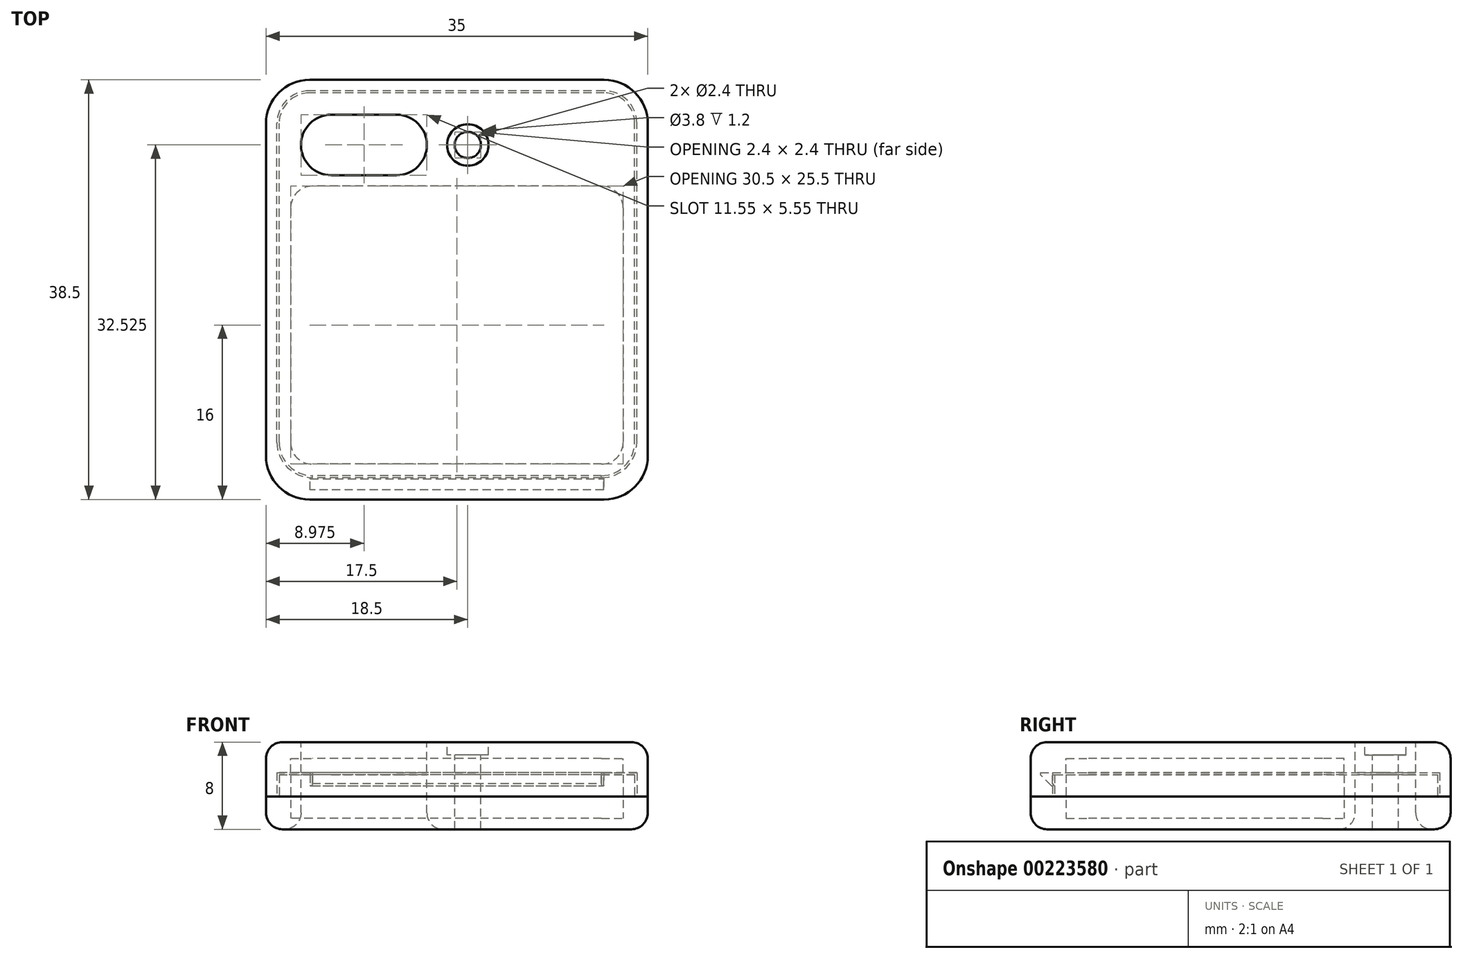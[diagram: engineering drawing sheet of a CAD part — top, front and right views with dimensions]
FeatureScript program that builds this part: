
annotation { "Feature Type Name" : "Feature", "Feature Type Description" : "" }
export const myFeature = defineFeature(function(context is Context, id is Id, definition is map)
    precondition{}
    {
        {
            var Q0;
            Q0=qCreatedBy(makeId("Top.planeOp"),FACE);
            var sketch = newSketch(context, id + "F0", { "sketchPlane" : qUnion([Q0])});
            skLineSegment(sketch, "E0.bottom", {"start": v(15, 12.5) * mm, "end": v(-15, 12.5) * mm, "construction": true});
            skLineSegment(sketch, "E0.top", {"start": v(15, -12.5) * mm, "end": v(-15, -12.5) * mm, "construction": true});
            skLineSegment(sketch, "E0.left", {"start": v(15, 12.5) * mm, "end": v(15, -12.5) * mm, "construction": true});
            skLineSegment(sketch, "E0.right", {"start": v(-15, 12.5) * mm, "end": v(-15, -12.5) * mm, "construction": true});
            skPoint(sketch, "E0.middle", {"position": v(0, 0) * mm});
            skLineSegment(sketch, "E1.bottom", {"start": v(13.5, -16) * mm, "end": v(-13.5, -16) * mm});
            skLineSegment(sketch, "E1.top", {"start": v(13.5, 22.5) * mm, "end": v(-13.5, 22.5) * mm});
            skLineSegment(sketch, "E1.left", {"start": v(17.5, -12) * mm, "end": v(17.5, 18.5) * mm});
            skLineSegment(sketch, "E1.right", {"start": v(-17.5, -12) * mm, "end": v(-17.5, 18.5) * mm});
            skPoint(sketch, "E1.middle", {"position": v(0, 3.25) * mm});
            skLineSegment(sketch, "E2.bottom", {"start": v(13.25, 12.75) * mm, "end": v(-13.25, 12.75) * mm});
            skLineSegment(sketch, "E2.top", {"start": v(13.25, -12.75) * mm, "end": v(-13.25, -12.75) * mm});
            skLineSegment(sketch, "E2.left", {"start": v(15.25, 10.75) * mm, "end": v(15.25, -10.75) * mm});
            skLineSegment(sketch, "E2.right", {"start": v(-15.25, 10.75) * mm, "end": v(-15.25, -10.75) * mm});
            skPoint(sketch, "E3.visualSharp", {"position": v(15.25, -12.75) * mm});
            skArc(sketch, "E3.filletArc", {"start": v(13.25, -12.75) * mm, "mid": v(14.66, -12.16) * mm, "end": v(15.25, -10.75) * mm});
            skPoint(sketch, "E4.visualSharp", {"position": v(-15.25, -12.75) * mm});
            skArc(sketch, "E4.filletArc", {"start": v(-15.25, -10.75) * mm, "mid": v(-14.66, -12.16) * mm, "end": v(-13.25, -12.75) * mm});
            skPoint(sketch, "E5.visualSharp", {"position": v(15.25, 12.75) * mm});
            skArc(sketch, "E5.filletArc", {"start": v(15.25, 10.75) * mm, "mid": v(14.66, 12.16) * mm, "end": v(13.25, 12.75) * mm});
            skPoint(sketch, "E6.visualSharp", {"position": v(-15.25, 12.75) * mm});
            skArc(sketch, "E6.filletArc", {"start": v(-13.25, 12.75) * mm, "mid": v(-14.66, 12.16) * mm, "end": v(-15.25, 10.75) * mm});
            skPoint(sketch, "E7.visualSharp", {"position": v(-17.5, -16) * mm});
            skArc(sketch, "E7.filletArc", {"start": v(-17.5, -12) * mm, "mid": v(-16.33, -14.83) * mm, "end": v(-13.5, -16) * mm});
            skPoint(sketch, "E8.visualSharp", {"position": v(17.5, -16) * mm});
            skArc(sketch, "E8.filletArc", {"start": v(13.5, -16) * mm, "mid": v(16.33, -14.83) * mm, "end": v(17.5, -12) * mm});
            skPoint(sketch, "E9.visualSharp", {"position": v(17.5, 22.5) * mm});
            skArc(sketch, "E9.filletArc", {"start": v(17.5, 18.5) * mm, "mid": v(16.33, 21.33) * mm, "end": v(13.5, 22.5) * mm});
            skPoint(sketch, "E10.visualSharp", {"position": v(-17.5, 22.5) * mm});
            skArc(sketch, "E10.filletArc", {"start": v(-13.5, 22.5) * mm, "mid": v(-16.33, 21.33) * mm, "end": v(-17.5, 18.5) * mm});
            skSolve(sketch);
        }
        {
            var Q0;
            Q0 = qSketchRegion(id + "F0", true);
            extrude(context, id + "F1", {"entities" : qUnion([Q0]), "depth" : 2 * mm});
        }
        {
            var Q0;
            Q0=makeQuery(id+"F1.opExtrude","CAP_FACE",FACE,{"disambiguationData":[OSD([sQuery(id+"F0.wireOp",EDGE,"E1.bottom"),sQuery(id+"F0.wireOp",EDGE,"E1.top"),sQuery(id+"F0.wireOp",EDGE,"E1.left"),sQuery(id+"F0.wireOp",EDGE,"E1.right"),sQuery(id+"F0.wireOp",EDGE,"E2.bottom"),sQuery(id+"F0.wireOp",EDGE,"E2.top"),sQuery(id+"F0.wireOp",EDGE,"E2.left"),sQuery(id+"F0.wireOp",EDGE,"E2.right"),sQuery(id+"F0.wireOp",EDGE,"E3.filletArc"),sQuery(id+"F0.wireOp",EDGE,"E4.filletArc"),sQuery(id+"F0.wireOp",EDGE,"E5.filletArc"),sQuery(id+"F0.wireOp",EDGE,"E6.filletArc"),sQuery(id+"F0.wireOp",EDGE,"E7.filletArc"),sQuery(id+"F0.wireOp",EDGE,"E8.filletArc"),sQuery(id+"F0.wireOp",EDGE,"E9.filletArc"),sQuery(id+"F0.wireOp",EDGE,"E10.filletArc")])],"isStart":true});
            var sketch = newSketch(context, id + "F2", { "sketchPlane" : qUnion([Q0])});
            skArc(sketch, "E11.0", {"start": v(17.5, -18.5) * mm, "mid": v(16.33, -21.33) * mm, "end": v(13.5, -22.5) * mm});
            skLineSegment(sketch, "E11.1", {"start": v(17.5, 12) * mm, "end": v(17.5, -18.5) * mm});
            skLineSegment(sketch, "E11.2", {"start": v(13.5, -22.5) * mm, "end": v(-13.5, -22.5) * mm});
            skArc(sketch, "E11.3", {"start": v(13.5, 16) * mm, "mid": v(16.33, 14.83) * mm, "end": v(17.5, 12) * mm});
            skArc(sketch, "E11.4", {"start": v(-13.5, -22.5) * mm, "mid": v(-16.33, -21.33) * mm, "end": v(-17.5, -18.5) * mm});
            skLineSegment(sketch, "E11.5", {"start": v(-17.5, 12) * mm, "end": v(-17.5, -18.5) * mm});
            skArc(sketch, "E11.6", {"start": v(-17.5, 12) * mm, "mid": v(-16.33, 14.83) * mm, "end": v(-13.5, 16) * mm});
            skLineSegment(sketch, "E11.7", {"start": v(13.5, 16) * mm, "end": v(-13.5, 16) * mm});
            skSolve(sketch);
        }
        {
            var Q0;
            Q0 = qSketchRegion(id + "F2", true);
            extrude(context, id + "F3", {"entities" : qUnion([Q0]), "operationType" : NewBodyOperationType.ADD, "depth" : 1 * mm});
        }
        {
            var Q0;
            Q0=makeQuery(id+"F1.opExtrude","CAP_FACE",FACE,{"disambiguationData":[OSD([sQuery(id+"F0.wireOp",EDGE,"E1.bottom"),sQuery(id+"F0.wireOp",EDGE,"E1.top"),sQuery(id+"F0.wireOp",EDGE,"E1.left"),sQuery(id+"F0.wireOp",EDGE,"E1.right"),sQuery(id+"F0.wireOp",EDGE,"E2.bottom"),sQuery(id+"F0.wireOp",EDGE,"E2.top"),sQuery(id+"F0.wireOp",EDGE,"E2.left"),sQuery(id+"F0.wireOp",EDGE,"E2.right"),sQuery(id+"F0.wireOp",EDGE,"E3.filletArc"),sQuery(id+"F0.wireOp",EDGE,"E4.filletArc"),sQuery(id+"F0.wireOp",EDGE,"E5.filletArc"),sQuery(id+"F0.wireOp",EDGE,"E6.filletArc"),sQuery(id+"F0.wireOp",EDGE,"E7.filletArc"),sQuery(id+"F0.wireOp",EDGE,"E8.filletArc"),sQuery(id+"F0.wireOp",EDGE,"E9.filletArc"),sQuery(id+"F0.wireOp",EDGE,"E10.filletArc")])],"isStart":false});
            var sketch = newSketch(context, id + "F4", { "sketchPlane" : qUnion([Q0])});
            skArc(sketch, "E12.0", {"start": v(16.3, 18.5) * mm, "mid": v(15.48, 20.48) * mm, "end": v(13.5, 21.3) * mm});
            skLineSegment(sketch, "E12.1", {"start": v(16.3, -10.75) * mm, "end": v(16.3, 18.5) * mm});
            skLineSegment(sketch, "E12.2", {"start": v(13.5, 21.3) * mm, "end": v(-13.5, 21.3) * mm});
            skArc(sketch, "E12.4", {"start": v(-13.5, 21.3) * mm, "mid": v(-15.48, 20.48) * mm, "end": v(-16.3, 18.5) * mm});
            skLineSegment(sketch, "E12.5", {"start": v(-16.3, -10.75) * mm, "end": v(-16.3, 18.5) * mm});
            skArc(sketch, "E13.0", {"start": v(15.25, 10.75) * mm, "mid": v(14.66, 12.16) * mm, "end": v(13.25, 12.75) * mm});
            skLineSegment(sketch, "E13.1", {"start": v(15.25, 10.75) * mm, "end": v(15.25, -10.75) * mm});
            skLineSegment(sketch, "E13.2", {"start": v(13.25, 12.75) * mm, "end": v(-13.25, 12.75) * mm});
            skArc(sketch, "E13.3", {"start": v(13.25, -12.75) * mm, "mid": v(14.66, -12.16) * mm, "end": v(15.25, -10.75) * mm});
            skArc(sketch, "E13.4", {"start": v(-13.25, 12.75) * mm, "mid": v(-14.66, 12.16) * mm, "end": v(-15.25, 10.75) * mm});
            skLineSegment(sketch, "E13.5", {"start": v(-15.25, 10.75) * mm, "end": v(-15.25, -10.75) * mm});
            skArc(sketch, "E13.6", {"start": v(-15.25, -10.75) * mm, "mid": v(-14.66, -12.16) * mm, "end": v(-13.25, -12.75) * mm});
            skLineSegment(sketch, "E13.7", {"start": v(13.25, -12.75) * mm, "end": v(-13.25, -12.75) * mm});
            skArc(sketch, "E14.0", {"start": v(13.25, -13.8) * mm, "mid": v(15.4, -12.9) * mm, "end": v(16.3, -10.75) * mm});
            skLineSegment(sketch, "E14.1", {"start": v(13.25, -13.8) * mm, "end": v(-13.25, -13.8) * mm});
            skArc(sketch, "E14.2", {"start": v(-16.3, -10.75) * mm, "mid": v(-15.4, -12.9) * mm, "end": v(-13.25, -13.8) * mm});
            skSolve(sketch);
        }
        {
            var Q0;
            Q0 = qSketchRegion(id + "F4", true);
            extrude(context, id + "F5", {"entities" : qUnion([Q0]), "operationType" : NewBodyOperationType.ADD, "depth" : 2 * mm});
        }
        {
            var Q0;
            Q0=makeQuery(id+"F5.opExtrude","SWEPT_FACE",FACE,{"disambiguationData":[OSD([sQuery(id+"F4.wireOp",EDGE,"E14.1")])]});
            var sketch = newSketch(context, id + "F6", { "sketchPlane" : qUnion([Q0])});
            skLineSegment(sketch, "E15.bottom", {"start": v(-13.25, 4) * mm, "end": v(13.25, 4) * mm});
            skLineSegment(sketch, "E15.top", {"start": v(-13.25, 3) * mm, "end": v(13.25, 3) * mm});
            skLineSegment(sketch, "E15.left", {"start": v(-13.25, 4) * mm, "end": v(-13.25, 3) * mm});
            skLineSegment(sketch, "E15.right", {"start": v(13.25, 4) * mm, "end": v(13.25, 3) * mm});
            skSolve(sketch);
        }
        {
            var Q0;
            Q0 = qSketchRegion(id + "F6", true);
            extrude(context, id + "F7", {"entities" : qUnion([Q0]), "operationType" : NewBodyOperationType.ADD, "depth" : .5 * mm});
        }
        {
            var Q0;
            Q0=makeQuery(id+"F7.opExtrude","CAP_EDGE",EDGE,{"disambiguationData":[OSD([sQuery(id+"F6.wireOp",EDGE,"E15.top")])],"isStart":false});
            chamfer(context, id + "F8", {"entities" : qUnion([Q0]), "width" : .5 * mm, "tangentPropagation" : true});
        }
        {
            var Q0;
            Q0=makeQuery(id+"F1.opExtrude","CAP_FACE",FACE,{"disambiguationData":[OSD([sQuery(id+"F0.wireOp",EDGE,"E1.bottom"),sQuery(id+"F0.wireOp",EDGE,"E1.top"),sQuery(id+"F0.wireOp",EDGE,"E1.left"),sQuery(id+"F0.wireOp",EDGE,"E1.right"),sQuery(id+"F0.wireOp",EDGE,"E2.bottom"),sQuery(id+"F0.wireOp",EDGE,"E2.top"),sQuery(id+"F0.wireOp",EDGE,"E2.left"),sQuery(id+"F0.wireOp",EDGE,"E2.right"),sQuery(id+"F0.wireOp",EDGE,"E3.filletArc"),sQuery(id+"F0.wireOp",EDGE,"E4.filletArc"),sQuery(id+"F0.wireOp",EDGE,"E5.filletArc"),sQuery(id+"F0.wireOp",EDGE,"E6.filletArc"),sQuery(id+"F0.wireOp",EDGE,"E7.filletArc"),sQuery(id+"F0.wireOp",EDGE,"E8.filletArc"),sQuery(id+"F0.wireOp",EDGE,"E9.filletArc"),sQuery(id+"F0.wireOp",EDGE,"E10.filletArc")])],"isStart":false});
            var sketch = newSketch(context, id + "F9", { "sketchPlane" : qUnion([Q0])});
            skLineSegment(sketch, "E16.0", {"start": v(-17.5, -12) * mm, "end": v(-17.5, 18.5) * mm});
            skArc(sketch, "E16.1", {"start": v(-13.5, 22.5) * mm, "mid": v(-16.33, 21.33) * mm, "end": v(-17.5, 18.5) * mm});
            skArc(sketch, "E16.2", {"start": v(-17.5, -12) * mm, "mid": v(-16.33, -14.83) * mm, "end": v(-13.5, -16) * mm});
            skLineSegment(sketch, "E16.3", {"start": v(13.5, 22.5) * mm, "end": v(-13.5, 22.5) * mm});
            skLineSegment(sketch, "E16.4", {"start": v(13.5, -16) * mm, "end": v(-13.5, -16) * mm});
            skArc(sketch, "E16.5", {"start": v(13.5, -16) * mm, "mid": v(16.33, -14.83) * mm, "end": v(17.5, -12) * mm});
            skLineSegment(sketch, "E16.6", {"start": v(17.5, -12) * mm, "end": v(17.5, 18.5) * mm});
            skArc(sketch, "E16.7", {"start": v(17.5, 18.5) * mm, "mid": v(16.33, 21.33) * mm, "end": v(13.5, 22.5) * mm});
            skLineSegment(sketch, "E17.0", {"start": v(-16.5, -10.75) * mm, "end": v(-16.5, 18.5) * mm});
            skArc(sketch, "E17.1", {"start": v(-13.5, 21.5) * mm, "mid": v(-15.62, 20.62) * mm, "end": v(-16.5, 18.5) * mm});
            skArc(sketch, "E17.2", {"start": v(-16.5, -10.75) * mm, "mid": v(-15.55, -13.05) * mm, "end": v(-13.25, -14) * mm});
            skLineSegment(sketch, "E17.3", {"start": v(13.5, 21.5) * mm, "end": v(-13.5, 21.5) * mm});
            skLineSegment(sketch, "E17.4", {"start": v(13.25, -14) * mm, "end": v(-13.25, -14) * mm});
            skArc(sketch, "E17.5", {"start": v(13.25, -14) * mm, "mid": v(15.55, -13.05) * mm, "end": v(16.5, -10.75) * mm});
            skLineSegment(sketch, "E17.6", {"start": v(16.5, -10.75) * mm, "end": v(16.5, 18.5) * mm});
            skArc(sketch, "E17.7", {"start": v(16.5, 18.5) * mm, "mid": v(15.62, 20.62) * mm, "end": v(13.5, 21.5) * mm});
            skSolve(sketch);
        }
        {
            var Q0;
            Q0 = qSketchRegion(id + "F9", true);
            extrude(context, id + "F10", {"entities" : qUnion([Q0]), "depth" : 3.5 * mm});
        }
        {
            var Q0;
            {var subQ2=sQuery(id+"F9.wireOp",EDGE,"E17.4");Q0=makeQuery(id+"F10.boolean.opBoolean","SPLIT",FACE,{"disambiguationData":[TD([makeQuery(id+"F7.opExtrude","SWEPT_FACE",FACE,{"disambiguationData":[OSD([sQuery(id+"F6.wireOp",EDGE,"E15.bottom")])]})])],"derivedFrom":makeQuery(id+"F10.opExtrude","SWEPT_FACE",FACE,{"disambiguationData":[OSD([subQ2])]})});}
            var sketch = newSketch(context, id + "F11", { "sketchPlane" : qUnion([Q0])});
            skLineSegment(sketch, "E18.0", {"start": v(13.45, 4.2) * mm, "end": v(13.45, 3) * mm});
            skLineSegment(sketch, "E18.1", {"start": v(-13.45, 4.2) * mm, "end": v(13.45, 4.2) * mm});
            skLineSegment(sketch, "E18.2", {"start": v(-13.45, 4.2) * mm, "end": v(-13.45, 3) * mm});
            skLineSegment(sketch, "E19", {"start": v(-13.45, 3) * mm, "end": v(13.45, 3) * mm});
            skSolve(sketch);
        }
        {
            var Q0;
            Q0 = qSketchRegion(id + "F11", true);
            extrude(context, id + "F12", {"entities" : qUnion([Q0]), "operationType" : NewBodyOperationType.REMOVE, "oppositeDirection" : true, "depth" : 1.1 * mm});
        }
        {
            var Q0;
            Q0=makeQuery(id+"F12.boolean.opBoolean","COPY",EDGE,{"derivedFrom":makeQuery(id+"F12.opExtrude","CAP_EDGE",EDGE,{"disambiguationData":[OSD([sQuery(id+"F11.wireOp",EDGE,"E19")])],"isStart":false})});
            chamfer(context, id + "F13", {"entities" : qUnion([Q0]), "width" : 1 * mm, "tangentPropagation" : true});
        }
        {
            var Q0;
            Q0=makeQuery(id+"F10.opExtrude","CAP_FACE",FACE,{"disambiguationData":[OSD([sQuery(id+"F9.wireOp",EDGE,"E16.0"),sQuery(id+"F9.wireOp",EDGE,"E16.1"),sQuery(id+"F9.wireOp",EDGE,"E16.2"),sQuery(id+"F9.wireOp",EDGE,"E16.3"),sQuery(id+"F9.wireOp",EDGE,"E16.4"),sQuery(id+"F9.wireOp",EDGE,"E16.5"),sQuery(id+"F9.wireOp",EDGE,"E16.6"),sQuery(id+"F9.wireOp",EDGE,"E16.7"),sQuery(id+"F9.wireOp",EDGE,"E17.0"),sQuery(id+"F9.wireOp",EDGE,"E17.1"),sQuery(id+"F9.wireOp",EDGE,"E17.2"),sQuery(id+"F9.wireOp",EDGE,"E17.3"),sQuery(id+"F9.wireOp",EDGE,"E17.4"),sQuery(id+"F9.wireOp",EDGE,"E17.5"),sQuery(id+"F9.wireOp",EDGE,"E17.6"),sQuery(id+"F9.wireOp",EDGE,"E17.7")])],"isStart":false});
            var sketch = newSketch(context, id + "F14", { "sketchPlane" : qUnion([Q0])});
            skArc(sketch, "E20.0", {"start": v(16.5, 18.5) * mm, "mid": v(15.62, 20.62) * mm, "end": v(13.5, 21.5) * mm});
            skLineSegment(sketch, "E20.1", {"start": v(16.5, -10.75) * mm, "end": v(16.5, 18.5) * mm});
            skLineSegment(sketch, "E20.2", {"start": v(13.5, 21.5) * mm, "end": v(-13.5, 21.5) * mm});
            skArc(sketch, "E20.3", {"start": v(13.25, -14) * mm, "mid": v(15.55, -13.05) * mm, "end": v(16.5, -10.75) * mm});
            skArc(sketch, "E20.4", {"start": v(-13.5, 21.5) * mm, "mid": v(-15.62, 20.62) * mm, "end": v(-16.5, 18.5) * mm});
            skLineSegment(sketch, "E20.5", {"start": v(-16.5, -10.75) * mm, "end": v(-16.5, 18.5) * mm});
            skArc(sketch, "E20.6", {"start": v(-16.5, -10.75) * mm, "mid": v(-15.55, -13.05) * mm, "end": v(-13.25, -14) * mm});
            skLineSegment(sketch, "E20.7", {"start": v(13.25, -14) * mm, "end": v(-13.25, -14) * mm});
            skArc(sketch, "E21.0", {"start": v(15.25, 10.75) * mm, "mid": v(14.66, 12.16) * mm, "end": v(13.25, 12.75) * mm});
            skLineSegment(sketch, "E21.1", {"start": v(15.25, 10.75) * mm, "end": v(15.25, -10.75) * mm});
            skLineSegment(sketch, "E21.2", {"start": v(13.25, 12.75) * mm, "end": v(-13.25, 12.75) * mm});
            skArc(sketch, "E21.3", {"start": v(13.25, -12.75) * mm, "mid": v(14.66, -12.16) * mm, "end": v(15.25, -10.75) * mm});
            skArc(sketch, "E21.4", {"start": v(-13.25, 12.75) * mm, "mid": v(-14.66, 12.16) * mm, "end": v(-15.25, 10.75) * mm});
            skLineSegment(sketch, "E21.5", {"start": v(-15.25, 10.75) * mm, "end": v(-15.25, -10.75) * mm});
            skArc(sketch, "E21.6", {"start": v(-15.25, -10.75) * mm, "mid": v(-14.66, -12.16) * mm, "end": v(-13.25, -12.75) * mm});
            skLineSegment(sketch, "E21.7", {"start": v(13.25, -12.75) * mm, "end": v(-13.25, -12.75) * mm});
            skSolve(sketch);
        }
        {
            var Q0;
            Q0 = qSketchRegion(id + "F14", true);
            var Q1;
            Q1=makeQuery(id+"F12.boolean.opBoolean","COPY",FACE,{"derivedFrom":makeQuery(id+"F12.opExtrude","SWEPT_FACE",FACE,{"disambiguationData":[OSD([sQuery(id+"F11.wireOp",EDGE,"E18.1")])]})});
            extrude(context, id + "F15", {"entities" : qUnion([Q0]), "operationType" : NewBodyOperationType.ADD, "endBound" : BoundingType.UP_TO_SURFACE, "oppositeDirection" : true, "endBoundEntityFace" : qUnion([Q1]), "depth" : 25 * mm});
        }
        {
            var Q0;
            Q0=makeQuery(id+"F15.boolean.opBoolean","MERGE",FACE,{"derivedFrom":[makeQuery(id+"F10.opExtrude","CAP_FACE",FACE,{"disambiguationData":[OSD([sQuery(id+"F9.wireOp",EDGE,"E16.0"),sQuery(id+"F9.wireOp",EDGE,"E16.1"),sQuery(id+"F9.wireOp",EDGE,"E16.2"),sQuery(id+"F9.wireOp",EDGE,"E16.3"),sQuery(id+"F9.wireOp",EDGE,"E16.4"),sQuery(id+"F9.wireOp",EDGE,"E16.5"),sQuery(id+"F9.wireOp",EDGE,"E16.6"),sQuery(id+"F9.wireOp",EDGE,"E16.7"),sQuery(id+"F9.wireOp",EDGE,"E17.0"),sQuery(id+"F9.wireOp",EDGE,"E17.1"),sQuery(id+"F9.wireOp",EDGE,"E17.2"),sQuery(id+"F9.wireOp",EDGE,"E17.3"),sQuery(id+"F9.wireOp",EDGE,"E17.4"),sQuery(id+"F9.wireOp",EDGE,"E17.5"),sQuery(id+"F9.wireOp",EDGE,"E17.6"),sQuery(id+"F9.wireOp",EDGE,"E17.7")])],"isStart":false}),makeQuery(id+"F15.opExtrude","CAP_FACE",FACE,{"disambiguationData":[OSD([sQuery(id+"F14.wireOp",EDGE,"E20.0"),sQuery(id+"F14.wireOp",EDGE,"E20.1"),sQuery(id+"F14.wireOp",EDGE,"E20.2"),sQuery(id+"F14.wireOp",EDGE,"E20.3"),sQuery(id+"F14.wireOp",EDGE,"E20.4"),sQuery(id+"F14.wireOp",EDGE,"E20.5"),sQuery(id+"F14.wireOp",EDGE,"E20.6"),sQuery(id+"F14.wireOp",EDGE,"E20.7"),sQuery(id+"F14.wireOp",EDGE,"E21.0"),sQuery(id+"F14.wireOp",EDGE,"E21.1"),sQuery(id+"F14.wireOp",EDGE,"E21.2"),sQuery(id+"F14.wireOp",EDGE,"E21.3"),sQuery(id+"F14.wireOp",EDGE,"E21.4"),sQuery(id+"F14.wireOp",EDGE,"E21.5"),sQuery(id+"F14.wireOp",EDGE,"E21.6"),sQuery(id+"F14.wireOp",EDGE,"E21.7")])],"isStart":true})]});
            var sketch = newSketch(context, id + "F16", { "sketchPlane" : qUnion([Q0])});
            skArc(sketch, "E22.0", {"start": v(17.5, 18.5) * mm, "mid": v(16.33, 21.33) * mm, "end": v(13.5, 22.5) * mm});
            skLineSegment(sketch, "E22.1", {"start": v(17.5, -12) * mm, "end": v(17.5, 18.5) * mm});
            skLineSegment(sketch, "E22.2", {"start": v(13.5, 22.5) * mm, "end": v(-13.5, 22.5) * mm});
            skArc(sketch, "E22.3", {"start": v(13.5, -16) * mm, "mid": v(16.33, -14.83) * mm, "end": v(17.5, -12) * mm});
            skArc(sketch, "E22.4", {"start": v(-13.5, 22.5) * mm, "mid": v(-16.33, 21.33) * mm, "end": v(-17.5, 18.5) * mm});
            skLineSegment(sketch, "E22.5", {"start": v(-17.5, -12) * mm, "end": v(-17.5, 18.5) * mm});
            skArc(sketch, "E22.6", {"start": v(-17.5, -12) * mm, "mid": v(-16.33, -14.83) * mm, "end": v(-13.5, -16) * mm});
            skLineSegment(sketch, "E22.7", {"start": v(13.5, -16) * mm, "end": v(-13.5, -16) * mm});
            skSolve(sketch);
        }
        {
            var Q0;
            Q0 = qSketchRegion(id + "F16", true);
            extrude(context, id + "F17", {"entities" : qUnion([Q0]), "operationType" : NewBodyOperationType.ADD, "depth" : 1.5 * mm});
        }
        {
            var Q0;
            Q0=makeQuery(id+"F17.opExtrude","CAP_FACE",FACE,{"disambiguationData":[OSD([sQuery(id+"F16.wireOp",EDGE,"E22.0"),sQuery(id+"F16.wireOp",EDGE,"E22.1"),sQuery(id+"F16.wireOp",EDGE,"E22.2"),sQuery(id+"F16.wireOp",EDGE,"E22.3"),sQuery(id+"F16.wireOp",EDGE,"E22.4"),sQuery(id+"F16.wireOp",EDGE,"E22.5"),sQuery(id+"F16.wireOp",EDGE,"E22.6"),sQuery(id+"F16.wireOp",EDGE,"E22.7")])],"isStart":false});
            var sketch = newSketch(context, id + "F18", { "sketchPlane" : qUnion([Q0])});
            skArc(sketch, "E23", {"start": v(-11.53, 19.3) * mm, "mid": v(-14.3, 16.53) * mm, "end": v(-11.53, 13.75) * mm});
            skLineSegment(sketch, "E24", {"start": v(-11.53, 16.53) * mm, "end": v(-5.53, 16.53) * mm, "construction": true});
            skArc(sketch, "E25", {"start": v(-5.53, 13.75) * mm, "mid": v(-2.75, 16.53) * mm, "end": v(-5.53, 19.3) * mm});
            skLineSegment(sketch, "E26", {"start": v(-11.53, 19.3) * mm, "end": v(-5.53, 19.3) * mm});
            skLineSegment(sketch, "E27", {"start": v(-11.53, 13.75) * mm, "end": v(-5.53, 13.75) * mm});
            skSolve(sketch);
        }
        {
            var Q0;
            Q0 = qSketchRegion(id + "F18", true);
            extrude(context, id + "F19", {"entities" : qUnion([Q0]), "operationType" : NewBodyOperationType.REMOVE, "endBound" : BoundingType.THROUGH_ALL, "oppositeDirection" : true, "depth" : 25 * mm});
        }
        {
            var Q0;
            Q0=makeQuery(id+"F17.opExtrude","CAP_FACE",FACE,{"disambiguationData":[OSD([sQuery(id+"F16.wireOp",EDGE,"E22.0"),sQuery(id+"F16.wireOp",EDGE,"E22.1"),sQuery(id+"F16.wireOp",EDGE,"E22.2"),sQuery(id+"F16.wireOp",EDGE,"E22.3"),sQuery(id+"F16.wireOp",EDGE,"E22.4"),sQuery(id+"F16.wireOp",EDGE,"E22.5"),sQuery(id+"F16.wireOp",EDGE,"E22.6"),sQuery(id+"F16.wireOp",EDGE,"E22.7")])],"isStart":false});
            var sketch = newSketch(context, id + "F20", { "sketchPlane" : qUnion([Q0])});
            skLineSegment(sketch, "E28", {"start": v(-2.75, 16.53) * mm, "end": v(17.5, 16.53) * mm, "construction": true});
            skPoint(sketch, "E28.endSnap0", {"position": v(-2.75, 16.52) * mm});
            skCircle(sketch, "E29", {"center": v(1, 16.53) * mm, "radius": 1.9 * mm});
            skSolve(sketch);
        }
        {
            var Q0;
            Q0 = qSketchRegion(id + "F20", true);
            extrude(context, id + "F21", {"entities" : qUnion([Q0]), "operationType" : NewBodyOperationType.REMOVE, "oppositeDirection" : true, "depth" : 1.2 * mm});
        }
        {
            var Q0;
            Q0=makeQuery(id+"F21.boolean.opBoolean","COPY",FACE,{"derivedFrom":makeQuery(id+"F21.opExtrude","CAP_FACE",FACE,{"disambiguationData":[OSD([sQuery(id+"F20.wireOp",EDGE,"E29")])],"isStart":false})});
            var sketch = newSketch(context, id + "F22", { "sketchPlane" : qUnion([Q0])});
            skCircle(sketch, "E30", {"center": v(1, 16.53) * mm, "radius": 1.2 * mm});
            skSolve(sketch);
        }
        {
            var Q0;
            Q0 = qSketchRegion(id + "F22", true);
            extrude(context, id + "F23", {"entities" : qUnion([Q0]), "operationType" : NewBodyOperationType.REMOVE, "endBound" : BoundingType.THROUGH_ALL, "oppositeDirection" : true, "depth" : 25 * mm});
        }
        {
            var Q0;
            Q0=makeQuery(id+"F7.boolean.opBoolean","MERGE",FACE,{"derivedFrom":[makeQuery(id+"F5.opExtrude","CAP_FACE",FACE,{"disambiguationData":[OSD([sQuery(id+"F4.wireOp",EDGE,"E12.0"),sQuery(id+"F4.wireOp",EDGE,"E12.1"),sQuery(id+"F4.wireOp",EDGE,"E12.2"),sQuery(id+"F4.wireOp",EDGE,"E12.4"),sQuery(id+"F4.wireOp",EDGE,"E12.5"),sQuery(id+"F4.wireOp",EDGE,"E13.0"),sQuery(id+"F4.wireOp",EDGE,"E13.1"),sQuery(id+"F4.wireOp",EDGE,"E13.2"),sQuery(id+"F4.wireOp",EDGE,"E13.3"),sQuery(id+"F4.wireOp",EDGE,"E13.4"),sQuery(id+"F4.wireOp",EDGE,"E13.5"),sQuery(id+"F4.wireOp",EDGE,"E13.6"),sQuery(id+"F4.wireOp",EDGE,"E13.7"),sQuery(id+"F4.wireOp",EDGE,"E14.0"),sQuery(id+"F4.wireOp",EDGE,"E14.1"),sQuery(id+"F4.wireOp",EDGE,"E14.2")])],"isStart":false}),makeQuery(id+"F7.opExtrude","SWEPT_FACE",FACE,{"disambiguationData":[OSD([sQuery(id+"F6.wireOp",EDGE,"E15.bottom")])]})]});
            var sketch = newSketch(context, id + "F24", { "sketchPlane" : qUnion([Q0])});
            skCircle(sketch, "E31", {"center": v(1, 16.53) * mm, "radius": 0.82 * mm});
            skSolve(sketch);
        }
        {
            var Q0;
            Q0 = qSketchRegion(id + "F24", true);
            extrude(context, id + "F25", {"entities" : qUnion([Q0]), "operationType" : NewBodyOperationType.REMOVE, "oppositeDirection" : true, "depth" : 6 * mm});
        }
        {
            var Q0;
            Q0=makeQuery(id+"F19.boolean.opBoolean","COPY",EDGE,{"derivedFrom":makeQuery(id+"F19.opExtrude","CAP_EDGE",EDGE,{"disambiguationData":[OSD([sQuery(id+"F18.wireOp",EDGE,"E26")])],"isStart":true})});
            var Q1;
            Q1=makeQuery(id+"F17.opExtrude","CAP_EDGE",EDGE,{"disambiguationData":[OSD([sQuery(id+"F16.wireOp",EDGE,"E22.5")])],"isStart":false});
            var Q2;
            Q2=makeQuery(id+"F3.opExtrude","CAP_EDGE",EDGE,{"disambiguationData":[OSD([sQuery(id+"F2.wireOp",EDGE,"E11.5")])],"isStart":false});
            var Q3;
            Q3=makeQuery(id+"F19.boolean.opBoolean","INTERSECT",EDGE,{"derivedFrom":[makeQuery(id+"F3.opExtrude","CAP_FACE",FACE,{"disambiguationData":[OSD([sQuery(id+"F2.wireOp",EDGE,"E11.0"),sQuery(id+"F2.wireOp",EDGE,"E11.1"),sQuery(id+"F2.wireOp",EDGE,"E11.2"),sQuery(id+"F2.wireOp",EDGE,"E11.3"),sQuery(id+"F2.wireOp",EDGE,"E11.4"),sQuery(id+"F2.wireOp",EDGE,"E11.5"),sQuery(id+"F2.wireOp",EDGE,"E11.6"),sQuery(id+"F2.wireOp",EDGE,"E11.7")])],"isStart":false}),makeQuery(id+"F19.opExtrude","SWEPT_FACE",FACE,{"disambiguationData":[OSD([sQuery(id+"F18.wireOp",EDGE,"E27")])]})]});
            fillet(context, id + "F26", {"entities" : qUnion([Q0, Q1, Q2, Q3]), "radius" : 1.5 * mm, "tangentPropagation" : true, "allowEdgeOverflow" : false});
        }
    });
